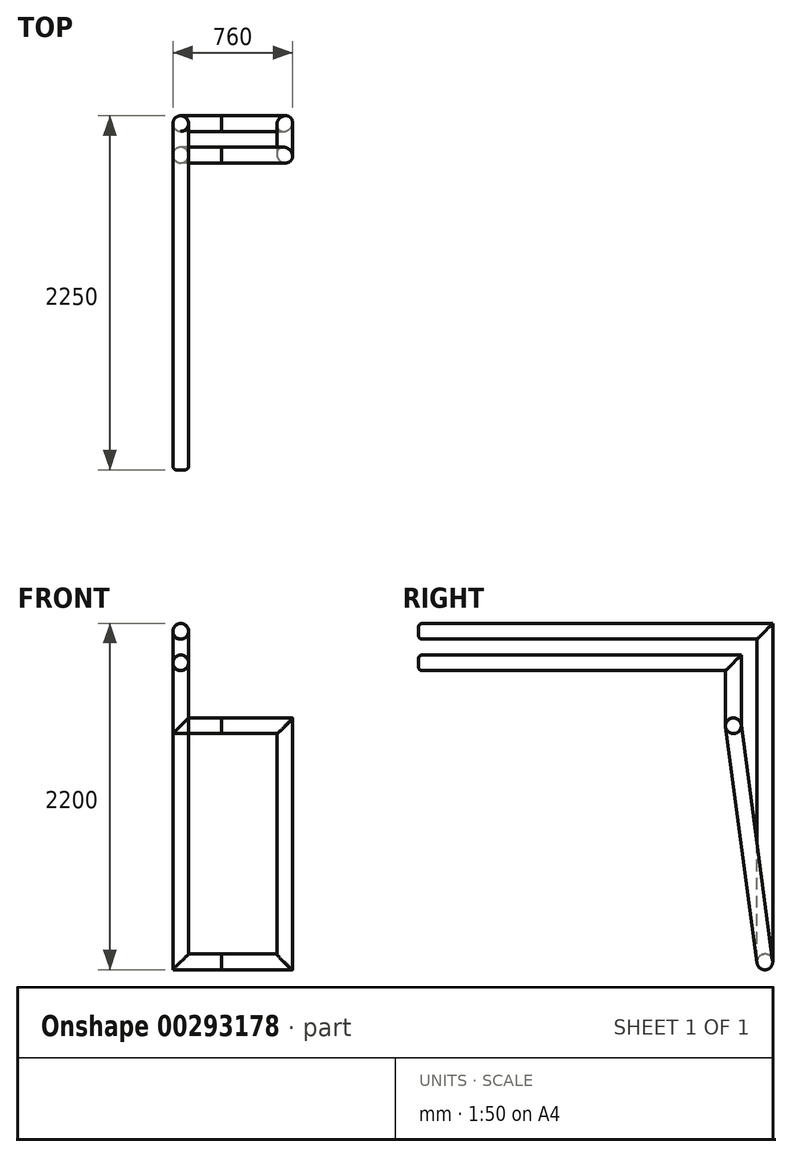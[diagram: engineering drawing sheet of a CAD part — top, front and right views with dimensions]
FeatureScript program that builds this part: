
annotation { "Feature Type Name" : "Feature", "Feature Type Description" : "" }
export const myFeature = defineFeature(function(context is Context, id is Id, definition is map)
    precondition{}
    {
        {
            var Q0;
            Q0=qCreatedBy(makeId("Front.planeOp"),FACE);
            var sketch = newSketch(context, id + "F0", { "sketchPlane" : qUnion([Q0])});
            skLineSegment(sketch, "E0", {"start": v(0, 0) * mm, "end": v(-260, 0) * mm});
            skLineSegment(sketch, "E1", {"start": v(-260, 0) * mm, "end": v(-260, 400) * mm});
            skSolve(sketch);
        }
        {
            var Q0;
            Q0=qCreatedBy(makeId("Right.planeOp"),FACE);
            var sketch = newSketch(context, id + "F1", { "sketchPlane" : qUnion([Q0])});
            skCircle(sketch, "E2", {"center": v(0, 0) * mm, "radius": 50 * mm});
            skSolve(sketch);
        }
        {
            var Q0;
            Q0=qCreatedBy(makeId("Top.planeOp"),FACE);
            var Q1;
            Q1=sQuery(id+"F0.wireOp",VERTEX,"E1.end");
            cPlane(context, id + "F2", {"entities" : qUnion([Q0, Q1]), "cplaneType" : CPlaneType.PLANE_POINT, "offset" : 25 * mm, "width" : 150 * mm, "height" : 150 * mm});
        }
        {
            var Q0;
            Q0=qCreatedBy(id+"F2.planeOp",FACE);
            var sketch = newSketch(context, id + "F3", { "sketchPlane" : qUnion([Q0])});
            skLineSegment(sketch, "E3", {"start": v(-260, 0) * mm, "end": v(-260, -2000) * mm});
            skSolve(sketch);
        }
        {
            var Q0;
            Q0=makeQuery(id+"F1.imprint","IMPRINT",FACE,{"disambiguationData":[TD([[makeQuery(id+"F1.imprint","IMPRINT",EDGE,{"derivedFrom":sQuery(id+"F1.wireOp",EDGE,"E2")}),1.0]])]});
            var Q1;
            Q1 = qSketchRegion(id + "F0", true);
            var Q2;
            Q2=sQuery(id+"F0.wireOp",EDGE,"E0");
            var Q3;
            Q3=sQuery(id+"F0.wireOp",EDGE,"E1");
            var Q4;
            Q4=sQuery(id+"F3.wireOp",EDGE,"E3");
            var Q5;
            Q5=sQuery(id+"F3.wireOp",EDGE,"rmcMWpX5-u5BM-HzK1-xHus-mWQfbpHTWt7I");
            var Q6;
            Q6=sQuery(id+"F3.wireOp",EDGE,"VScGvmaz-WYDr-emek-IFvg-DusYobt6PAtu");
            sweep(context, id + "F4", {"profiles" : qUnion([Q0, Q1]), "path" : qUnion([Q2, Q3, Q4, Q5, Q6])});
        }
        {
            var Q0;
            Q0=qCreatedBy(makeId("Front.planeOp"),FACE);
            cPlane(context, id + "F5", {"entities" : qUnion([Q0]), "cplaneType" : CPlaneType.OFFSET, "offset" : 200 * mm, "oppositeDirection" : true, "width" : 150 * mm, "height" : 150 * mm});
        }
        {
            var Q0;
            Q0=qCreatedBy(id+"F5.planeOp",FACE);
            var sketch = newSketch(context, id + "F6", { "sketchPlane" : qUnion([Q0])});
            skLineSegment(sketch, "E4", {"start": v(0, -1500) * mm, "end": v(-260, -1500) * mm});
            skLineSegment(sketch, "E5", {"start": v(-260, -1500) * mm, "end": v(-260, 600) * mm});
            skSolve(sketch);
        }
        {
            var Q0;
            Q0=qCreatedBy(makeId("Top.planeOp"),FACE);
            var Q1;
            Q1=sQuery(id+"F6.wireOp",VERTEX,"E5.end");
            cPlane(context, id + "F7", {"entities" : qUnion([Q0, Q1]), "cplaneType" : CPlaneType.PLANE_POINT, "offset" : 25 * mm, "width" : 150 * mm, "height" : 150 * mm});
        }
        {
            var Q0;
            Q0=qCreatedBy(id+"F7.planeOp",FACE);
            var sketch = newSketch(context, id + "F8", { "sketchPlane" : qUnion([Q0])});
            skLineSegment(sketch, "E6", {"start": v(-260, 200) * mm, "end": v(-260, -2000) * mm});
            skSolve(sketch);
        }
        {
            var Q0;
            Q0=qCreatedBy(makeId("Right.planeOp"),FACE);
            var Q1;
            Q1=sQuery(id+"F6.wireOp",VERTEX,"E4.start");
            cPlane(context, id + "F9", {"entities" : qUnion([Q0, Q1]), "cplaneType" : CPlaneType.PLANE_POINT, "offset" : 25 * mm, "width" : 150 * mm, "height" : 150 * mm});
        }
        {
            var Q0;
            Q0=qCreatedBy(id+"F9.planeOp",FACE);
            var sketch = newSketch(context, id + "F10", { "sketchPlane" : qUnion([Q0])});
            skCircle(sketch, "E7", {"center": v(200, -1500) * mm, "radius": 50 * mm});
            skLineSegment(sketch, "E8", {"start": v(200, -1500) * mm, "end": v(0, 0) * mm});
            skPoint(sketch, "E9", {"position": v(100, -750) * mm});
            skSolve(sketch);
        }
        {
            var Q0;
            Q0=makeQuery(id+"F10.imprint","IMPRINT",FACE,{"disambiguationData":[TD([[makeQuery(id+"F10.imprint","IMPRINT",EDGE,{"derivedFrom":sQuery(id+"F10.wireOp",EDGE,"E7")}),1.0]])]});
            var Q1;
            Q1=sQuery(id+"F6.wireOp",EDGE,"E4");
            var Q2;
            Q2=sQuery(id+"F6.wireOp",EDGE,"E5");
            var Q3;
            Q3=sQuery(id+"F8.wireOp",EDGE,"E6");
            sweep(context, id + "F11", {"profiles" : qUnion([Q0]), "path" : qUnion([Q1, Q2, Q3])});
        }
        {
            var Q0;
            Q0=qCreatedBy(makeId("Front.planeOp"),FACE);
            var sketch = newSketch(context, id + "F12", { "sketchPlane" : qUnion([Q0])});
            skPoint(sketch, "E10", {"position": v(37.04, 0) * mm});
            skSolve(sketch);
        }
        {
            var Q0;
            Q0=sQuery(id+"F10.wireOp",VERTEX,"E9");
            var Q1;
            Q1=sQuery(id+"F10.wireOp",VERTEX,"E8.end");
            var Q2;
            Q2=sQuery(id+"F12.wireOp",VERTEX,"E10");
            cPlane(context, id + "F13", {"entities" : qUnion([Q0, Q1, Q2]), "cplaneType" : CPlaneType.THREE_POINT, "offset" : 25 * mm, "width" : 150 * mm, "height" : 150 * mm});
        }
        {
            var Q0;
            Q0=qCreatedBy(id+"F13.planeOp",FACE);
            var sketch = newSketch(context, id + "F14", { "sketchPlane" : qUnion([Q0])});
            skLineSegment(sketch, "E11", {"start": v(0, 0) * mm, "end": v(400, 0) * mm});
            skLineSegment(sketch, "E12", {"start": v(400, 0) * mm, "end": v(400, -1513.27) * mm});
            skLineSegment(sketch, "E13", {"start": v(400, -1513.27) * mm, "end": v(0, -1513.27) * mm});
            skSolve(sketch);
        }
        {
            var Q0;
            Q0=makeQuery(id+"F10.imprint","IMPRINT",FACE,{"disambiguationData":[TD([[makeQuery(id+"F10.imprint","IMPRINT",EDGE,{"derivedFrom":sQuery(id+"F10.wireOp",EDGE,"E7")}),1.0]])]});
            var Q1;
            Q1=sQuery(id+"F14.wireOp",EDGE,"E13");
            var Q2;
            Q2=sQuery(id+"F14.wireOp",EDGE,"E12");
            var Q3;
            Q3=sQuery(id+"F14.wireOp",EDGE,"E11");
            sweep(context, id + "F15", {"profiles" : qUnion([Q0]), "path" : qUnion([Q1, Q2, Q3])});
        }
        {
            var Q0;
            Q0=makeQuery(id+"F11.opSweep","CAP_EDGE",EDGE,{"disambiguationData":[OSD([sQuery(id+"F8.wireOp",VERTEX,"E6.end"),sQuery(id+"F10.wireOp",EDGE,"E7")])],"isStart":false});
            fillet(context, id + "F16", {"entities" : qUnion([Q0]), "radius" : 25 * mm, "tangentPropagation" : true, "allowEdgeOverflow" : false});
        }
        {
            var Q0;
            Q0=makeQuery(id+"F4.opSweep","CAP_EDGE",EDGE,{"disambiguationData":[OSD([sQuery(id+"F1.wireOp",EDGE,"E2"),sQuery(id+"F3.wireOp",VERTEX,"E3.end")])],"isStart":false});
            fillet(context, id + "F17", {"entities" : qUnion([Q0]), "radius" : 25 * mm, "tangentPropagation" : true, "allowEdgeOverflow" : false});
        }
    });
